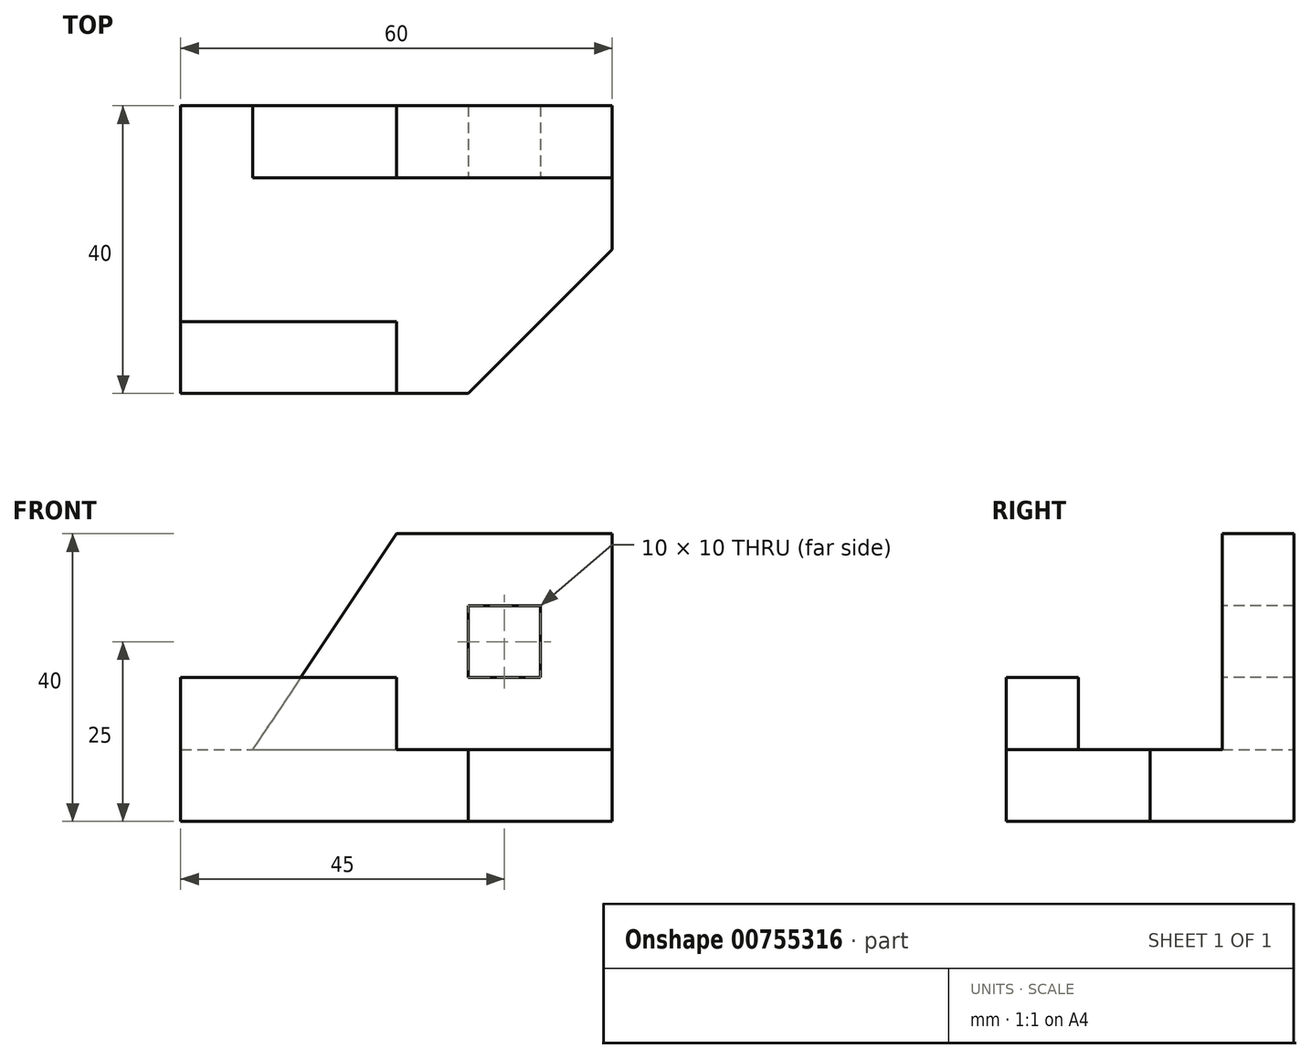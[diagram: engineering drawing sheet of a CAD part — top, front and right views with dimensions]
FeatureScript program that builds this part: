
annotation { "Feature Type Name" : "Feature", "Feature Type Description" : "" }
export const myFeature = defineFeature(function(context is Context, id is Id, definition is map)
    precondition{}
    {
        {
            var Q0;
            Q0=qCreatedBy(makeId("Front.planeOp"),FACE);
            var sketch = newSketch(context, id + "F0", { "sketchPlane" : qUnion([Q0])});
            skLineSegment(sketch, "E0", {"start": v(0, 0) * mm, "end": v(60, 0) * mm});
            skLineSegment(sketch, "E1", {"start": v(60, 0) * mm, "end": v(60, 40) * mm});
            skLineSegment(sketch, "E2", {"start": v(60, 40) * mm, "end": v(0, 40) * mm});
            skLineSegment(sketch, "E3", {"start": v(0, 40) * mm, "end": v(0, 0) * mm});
            skSolve(sketch);
        }
        {
            var Q0;
            Q0=makeQuery(id+"F0.imprint","IMPRINT",FACE,{"disambiguationData":[TD([[makeQuery(id+"F0.imprint","IMPRINT",EDGE,{"derivedFrom":sQuery(id+"F0.wireOp",EDGE,"E0")}),1.0]])]});
            extrude(context, id + "F1", {"entities" : qUnion([Q0]), "depth" : 40 * mm, "offsetDistance" : 25 * mm});
        }
        {
            var Q0;
            Q0=makeQuery(id+"F1.opExtrude","SWEPT_FACE",FACE,{"disambiguationData":[OSD([sQuery(id+"F0.wireOp",EDGE,"E1")])]});
            var sketch = newSketch(context, id + "F2", { "sketchPlane" : qUnion([Q0])});
            skLineSegment(sketch, "E4", {"start": v(0, 40) * mm, "end": v(-10, 40) * mm});
            skLineSegment(sketch, "E5", {"start": v(-10, 40) * mm, "end": v(-10, 10) * mm});
            skLineSegment(sketch, "E6", {"start": v(-10, 10) * mm, "end": v(-30, 10) * mm});
            skLineSegment(sketch, "E7", {"start": v(-30, 10) * mm, "end": v(-30, 20) * mm});
            skLineSegment(sketch, "E8", {"start": v(-30, 20) * mm, "end": v(-40, 20) * mm});
            skLineSegment(sketch, "E9", {"start": v(-40, 20) * mm, "end": v(-40, 40) * mm});
            skLineSegment(sketch, "E10", {"start": v(-40, 40) * mm, "end": v(-10, 40) * mm});
            skSolve(sketch);
        }
        {
            var Q0;
            Q0=makeQuery(id+"F2.imprint","IMPRINT",FACE,{"disambiguationData":[TD([[makeQuery(id+"F2.imprint","IMPRINT",EDGE,{"derivedFrom":sQuery(id+"F2.wireOp",EDGE,"E5")}),-1.0]])]});
            extrude(context, id + "F3", {"entities" : qUnion([Q0]), "operationType" : NewBodyOperationType.REMOVE, "oppositeDirection" : true, "depth" : 60 * mm, "offsetDistance" : 25 * mm});
        }
        {
            var Q0;
            Q0=makeQuery(id+"F3.boolean.opBoolean","COPY",FACE,{"derivedFrom":makeQuery(id+"F3.opExtrude","SWEPT_FACE",FACE,{"disambiguationData":[OSD([sQuery(id+"F2.wireOp",EDGE,"E8")])]})});
            var sketch = newSketch(context, id + "F4", { "sketchPlane" : qUnion([Q0])});
            skLineSegment(sketch, "E11", {"start": v(60, -30) * mm, "end": v(30, -30) * mm});
            skLineSegment(sketch, "E12", {"start": v(30, -30) * mm, "end": v(30, -40) * mm});
            skLineSegment(sketch, "E13", {"start": v(30, -40) * mm, "end": v(60, -40) * mm});
            skLineSegment(sketch, "E14", {"start": v(60, -40) * mm, "end": v(60, -30) * mm});
            skSolve(sketch);
        }
        {
            var Q0;
            Q0=makeQuery(id+"F4.imprint","IMPRINT",FACE,{"disambiguationData":[TD([[makeQuery(id+"F4.imprint","IMPRINT",EDGE,{"derivedFrom":sQuery(id+"F4.wireOp",EDGE,"E11")}),-1.0]])]});
            extrude(context, id + "F5", {"entities" : qUnion([Q0]), "operationType" : NewBodyOperationType.REMOVE, "oppositeDirection" : true, "depth" : 10 * mm, "offsetDistance" : 25 * mm});
        }
        {
            var Q0;
            Q0=makeQuery(id+"F5.boolean.opBoolean","MERGE",FACE,{"derivedFrom":[makeQuery(id+"F3.boolean.opBoolean","COPY",FACE,{"derivedFrom":makeQuery(id+"F3.opExtrude","SWEPT_FACE",FACE,{"disambiguationData":[OSD([sQuery(id+"F2.wireOp",EDGE,"E6")])]})}),makeQuery(id+"F5.opExtrude","CAP_FACE",FACE,{"disambiguationData":[OSD([sQuery(id+"F4.wireOp",EDGE,"E11"),sQuery(id+"F4.wireOp",EDGE,"E12"),sQuery(id+"F4.wireOp",EDGE,"E13"),sQuery(id+"F4.wireOp",EDGE,"E14")])],"isStart":false})]});
            var sketch = newSketch(context, id + "F6", { "sketchPlane" : qUnion([Q0])});
            skLineSegment(sketch, "E15", {"start": v(60, -40) * mm, "end": v(60, -20) * mm});
            skLineSegment(sketch, "E16", {"start": v(60, -20) * mm, "end": v(40, -40) * mm});
            skLineSegment(sketch, "E17", {"start": v(40, -40) * mm, "end": v(60, -40) * mm});
            skSolve(sketch);
        }
        {
            var Q0;
            Q0=makeQuery(id+"F6.imprint","IMPRINT",FACE,{"disambiguationData":[TD([[makeQuery(id+"F6.imprint","IMPRINT",EDGE,{"derivedFrom":sQuery(id+"F6.wireOp",EDGE,"E15")}),-1.0]])]});
            extrude(context, id + "F7", {"entities" : qUnion([Q0]), "operationType" : NewBodyOperationType.REMOVE, "oppositeDirection" : true, "depth" : 10 * mm, "offsetDistance" : 25 * mm});
        }
        {
            var Q0;
            Q0=makeQuery(id+"F1.opExtrude","CAP_FACE",FACE,{"disambiguationData":[OSD([sQuery(id+"F0.wireOp",EDGE,"E0"),sQuery(id+"F0.wireOp",EDGE,"E1"),sQuery(id+"F0.wireOp",EDGE,"E2"),sQuery(id+"F0.wireOp",EDGE,"E3")])],"isStart":true});
            var sketch = newSketch(context, id + "F8", { "sketchPlane" : qUnion([Q0])});
            skLineSegment(sketch, "E18", {"start": v(0, 0) * mm, "end": v(0, 10) * mm});
            skLineSegment(sketch, "E19", {"start": v(0, 10) * mm, "end": v(-10, 10) * mm});
            skLineSegment(sketch, "E20", {"start": v(-10, 10) * mm, "end": v(-30, 10) * mm});
            skLineSegment(sketch, "E21", {"start": v(-30, 10) * mm, "end": v(-30, 40) * mm});
            skLineSegment(sketch, "E22", {"start": v(-30, 40) * mm, "end": v(-10, 10) * mm});
            skSolve(sketch);
        }
        {
            var Q0;
            {var subQ0=sQuery(id+"F8.wireOp",EDGE,"E19");Q0=makeQuery(id+"F8.imprint","IMPRINT",FACE,{"disambiguationData":[TD([[makeQuery(id+"F8.imprint","IMPRINT",EDGE,{"derivedFrom":subQ0}),-1.0]])]});}
            extrude(context, id + "F9", {"entities" : qUnion([Q0]), "operationType" : NewBodyOperationType.REMOVE, "oppositeDirection" : true, "depth" : 10 * mm, "offsetDistance" : 25 * mm});
        }
        {
            var Q0;
            Q0=makeQuery(id+"F3.boolean.opBoolean","COPY",FACE,{"derivedFrom":makeQuery(id+"F3.opExtrude","SWEPT_FACE",FACE,{"disambiguationData":[OSD([sQuery(id+"F2.wireOp",EDGE,"E5")])]})});
            var sketch = newSketch(context, id + "F10", { "sketchPlane" : qUnion([Q0])});
            skLineSegment(sketch, "E23", {"start": v(60, 40) * mm, "end": v(50, 40) * mm});
            skLineSegment(sketch, "E24", {"start": v(50, 40) * mm, "end": v(50, 20) * mm});
            skLineSegment(sketch, "E25", {"start": v(50, 20) * mm, "end": v(40, 20) * mm});
            skLineSegment(sketch, "E26", {"start": v(40, 20) * mm, "end": v(40, 30) * mm});
            skLineSegment(sketch, "E27", {"start": v(40, 30) * mm, "end": v(50, 30) * mm});
            skSolve(sketch);
        }
        {
            var Q0;
            {var subQ0=sQuery(id+"F10.wireOp",EDGE,"E25");Q0=makeQuery(id+"F10.imprint","IMPRINT",FACE,{"disambiguationData":[TD([[makeQuery(id+"F10.imprint","IMPRINT",EDGE,{"derivedFrom":subQ0}),-1.0]])]});}
            extrude(context, id + "F11", {"entities" : qUnion([Q0]), "operationType" : NewBodyOperationType.REMOVE, "oppositeDirection" : true, "depth" : 10 * mm, "offsetDistance" : 25 * mm});
        }
    });
